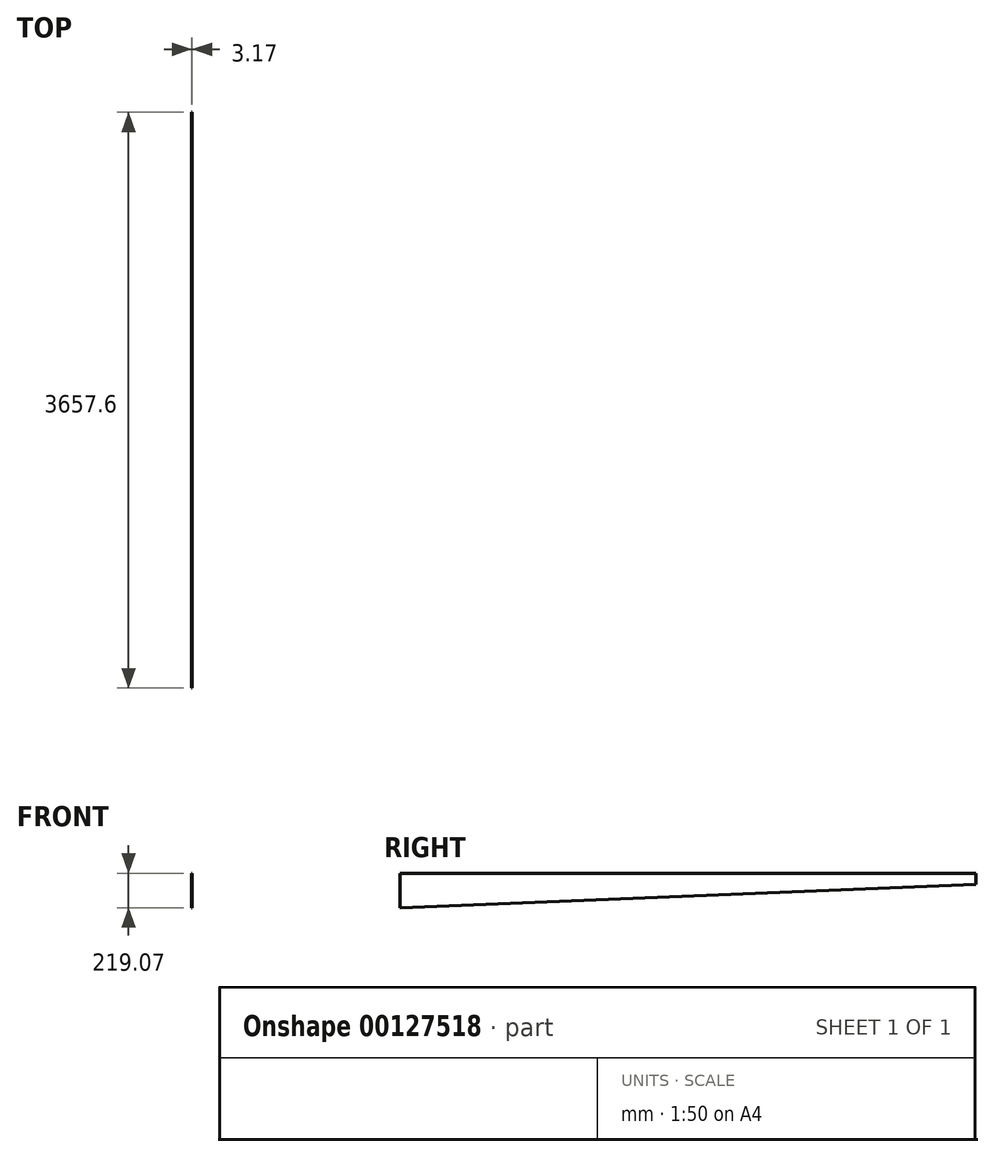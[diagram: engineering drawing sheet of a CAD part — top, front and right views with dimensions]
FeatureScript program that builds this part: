
annotation { "Feature Type Name" : "Feature", "Feature Type Description" : "" }
export const myFeature = defineFeature(function(context is Context, id is Id, definition is map)
    precondition{}
    {
        {
            var Q0;
            Q0=qCreatedBy(makeId("Right.planeOp"),FACE);
            var sketch = newSketch(context, id + "F0", { "sketchPlane" : qUnion([Q0])});
            skLineSegment(sketch, "E0", {"start": v(0, 0) * mm, "end": v(0, -219.08) * mm});
            skLineSegment(sketch, "E1", {"start": v(0, -219.08) * mm, "end": v(3657.6, -70.64) * mm});
            skLineSegment(sketch, "E2", {"start": v(3657.6, -70.64) * mm, "end": v(3657.6, 0) * mm});
            skLineSegment(sketch, "E3", {"start": v(3657.6, 0) * mm, "end": v(0, 0) * mm});
            skSolve(sketch);
        }
        {
            var Q0;
            Q0=qSketchRegion(id+"F0",true);
            extrude(context, id + "F1", {"entities" : qUnion([Q0]), "depth" : 3.17 * mm});
        }
    });
